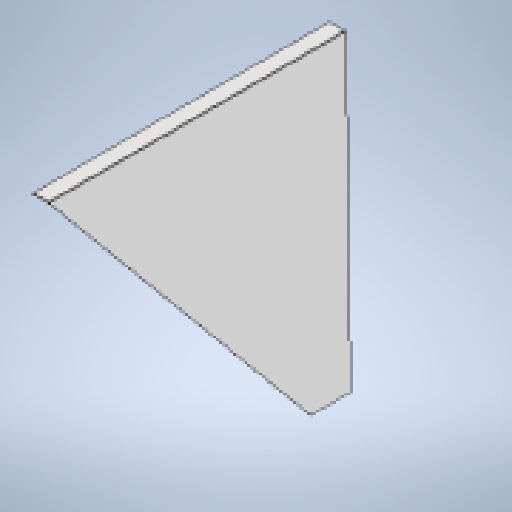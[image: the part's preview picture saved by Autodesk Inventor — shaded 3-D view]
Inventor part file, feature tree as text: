
AUTODESK INVENTOR PART (.ipt)
format: ipt  version: 2025 (Build 290162010, 162A)  size: 262,144 bytes
history: native  units: mm
features: other x5, sheet_metal_op x3, sketch x3, reference x2, extrude x1
ambient origin geometry x8: Origin, YZ Plane, XZ Plane, XY Plane, X Axis, Y Axis, Z Axis, Center Point
bodies: Body1 (feature_tree)
feature tree (14):
  sheet_metal_op  "Contour Flange2"
  extrude  "Extrusion13"  Depth=100.0mm
  other  "Mark2"
  sketch  "Sketch1"  dims[d0=1150.0mm d61=100.0mm]
  other  "Plate4"
  sheet_metal_op  "Bend4"
  sheet_metal_op  "Corner4"
  sketch  "Sketch17"  dims[d66=6.0mm]
  reference  "Reference1"
  reference  "Reference2"
  sketch  "Sketch19"  dims[d68=230.0mm d69=4.0mm d70=4.0mm d71=2.0mm d72=8.0mm d73=6.0mm d74=1500.0mm d75=6.0mm d76=4.0mm d77=16.0mm d78=4.0mm d79=6.0mm d83=855.0mm d87=20.666414mm d90=80.0mm d111=0.0mm d112=0.0mm d113=6.0mm]
  other  "ASY MSC 100 cone.iam"
  other  "MSC 114 cone IN right board.ipt:1"
  other  "MSC 113 cone IN left board.ipt:1"
